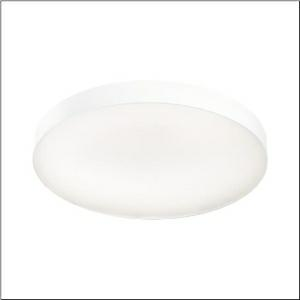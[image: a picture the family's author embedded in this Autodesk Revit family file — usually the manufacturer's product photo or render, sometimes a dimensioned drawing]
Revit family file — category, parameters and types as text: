
# Revit family: round_21_l_51mr38nd0421w
name_source: partatom
category: Lighting Fixtures
units: mm (PartAtom-declared; Revit-internal decimal feet)

## family parameters
Cut with Voids When Loaded = No
Host = Face
Light Source = No
Part Type = Normal
Room Calculation Point = No
Round Connector Dimension = Use Diameter
Shared = No

## types (1)
- Round 21 L (1 x LED, 12230 lm, 88.2 W, 4000K)
    Apparent Load = 88 VA
    CIE Flux Codes = 66 90 98 71 100
    Color Rendering = 80
    Color Temperature = 4000K
    Default Elevation = 1800 mm
    Description = Round 21 L, wall and ceiling luminaire, primary optical cover: micro prismatic cover, of PMMA, transparent, CAT 2 (L<= 3000cd/m²), light emission: direct/indirect distribution, primary light characteristic: symmetric, installation type: suspended mounting, surface-mounted, LED, rated luminous flux: 12.230lm, luminous efficacy: 139lm/W, light colour: 840, colour temperature: 4000K, control gear: DALI 2, with terminal, 5-pole, mains connection: 230V, AC, 50/60Hz, rated input power: 88W, housing, of aluminium, coated, white, diameter: 850mm, height: 62mm, protection rating (complete): IP40, insulation class (complete): insulation class I (protective earthing), certification: CE, impact resistance: IK04, permissible operating ambient temperature: -10..+35°C, packaging unit: 1 piece
    Height = 87 mm
    Lamp = 1 x LED
    Lamp Light Flux = 12230 lm
    Lamp Power = 88.2 W
    Lamp count = 1
    Length = 850 mm
    Luminous efficacy = 139 lm/W
    Manufacturer = Siteco
    ModVariant = No
    Model = 51MR38ND0421W
    Mounting Place = Ceiling
    Mounting Type = Surface mounted
    Number of Poles = 1
    OnlyDefault = Yes
    Power Factor = 1
    Product Name = Round 21 L
    Product group = wall and ceiling luminaire
    ProductGroupID = 304
    Protection Class = Protection class I
    Protection Degree = IP 40
    RLX_Detail_Level = 1
    RLX_Emergency_Light_Flux = 0 lm
    RLX_Emergency_Type = 0
    RLX_Emergency_Type_DB = No
    RlxData = <blob elided: 19497 chars, md5=9aa0ccc9>
    Socket = socket
    Standby Power = 0 W
    System Light Flux = 12230 lm
    System Power = 88 W
    Type Comments = Product without accessories
    Type Image = l_1258318.jpg
    URL = http://relux.com
    VarID = ---
    Voltage = 0 V
    Weight = 0.00 kg
    Width = 0 mm  [stored 0 ft]

note: [stored X ft] marks values corroborated as IEEE doubles in the binary element streams (Revit-internal decimal feet)

## geometry (parser evidence)
native form markers: Blend x4, Sweep x12
no freeform markers — native parametric forms only
